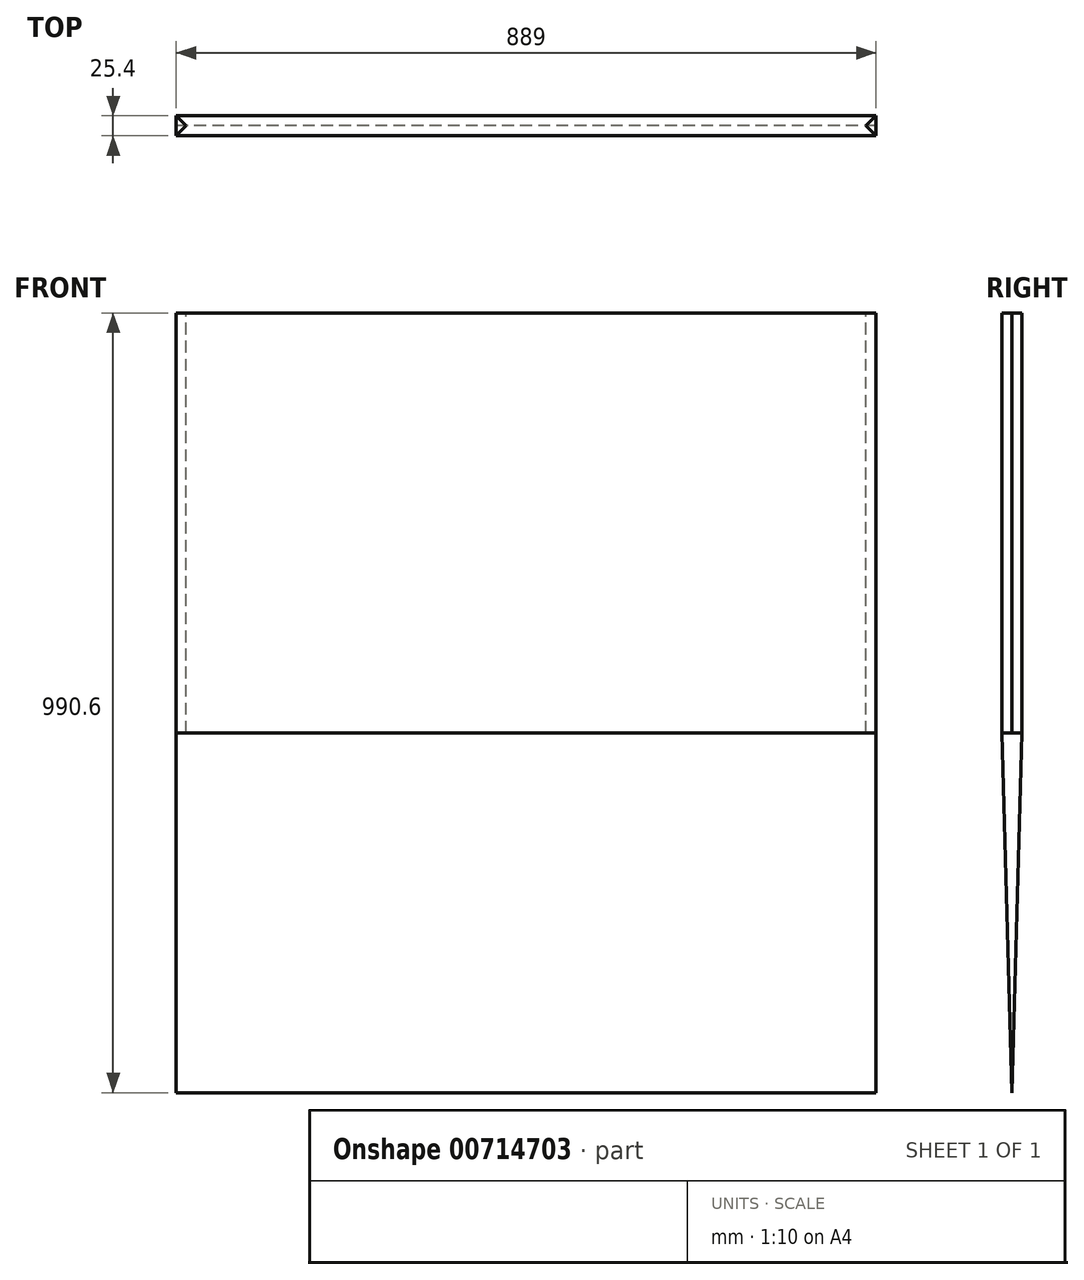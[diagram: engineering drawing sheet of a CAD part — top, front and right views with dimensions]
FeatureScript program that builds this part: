
annotation { "Feature Type Name" : "Feature", "Feature Type Description" : "" }
export const myFeature = defineFeature(function(context is Context, id is Id, definition is map)
    precondition{}
    {
        {
            var Q0;
            Q0=qCreatedBy(makeId("Top.planeOp"),FACE);
            var sketch = newSketch(context, id + "F0", { "sketchPlane" : qUnion([Q0])});
            skLineSegment(sketch, "E0", {"start": v(0, 25.4) * mm, "end": v(889, 25.4) * mm});
            skLineSegment(sketch, "E1", {"start": v(889, 25.4) * mm, "end": v(876.3, 12.7) * mm});
            skLineSegment(sketch, "E2", {"start": v(876.3, 12.7) * mm, "end": v(889, 0) * mm});
            skLineSegment(sketch, "E3", {"start": v(889, 0) * mm, "end": v(0, 0) * mm});
            skLineSegment(sketch, "E4", {"start": v(0, 0) * mm, "end": v(12.7, 12.7) * mm});
            skLineSegment(sketch, "E5", {"start": v(12.7, 12.7) * mm, "end": v(0, 25.4) * mm});
            skLineSegment(sketch, "E6", {"start": v(0, 25.4) * mm, "end": v(127, 25.4) * mm});
            skSolve(sketch);
        }
        {
            var Q0;
            Q0=makeQuery(id+"F0.imprint","IMPRINT",FACE,{"disambiguationData":[TD([[makeQuery(id+"F0.imprint","IMPRINT",EDGE,{"derivedFrom":sQuery(id+"F0.wireOp",EDGE,"E1")}),-1.0]])]});
            extrude(context, id + "F1", {"entities" : qUnion([Q0]), "oppositeDirection" : true, "depth" : 533.4 * mm, "offsetDistance" : 25.4 * mm});
        }
        {
            var Q0;
            Q0=qCreatedBy(makeId("Right.planeOp"),FACE);
            var sketch = newSketch(context, id + "F2", { "sketchPlane" : qUnion([Q0])});
            skLineSegment(sketch, "E7", {"start": v(0, -533.4) * mm, "end": v(25.4, -533.4) * mm});
            skLineSegment(sketch, "E8", {"start": v(25.4, -533.4) * mm, "end": v(12.7, -990.6) * mm});
            skLineSegment(sketch, "E9", {"start": v(12.7, -990.6) * mm, "end": v(0, -533.4) * mm});
            skSolve(sketch);
        }
        {
            var Q0;
            Q0 = qSketchRegion(id + "F2", true);
            var Q1;
            Q1=makeQuery(id+"F2.imprint","IMPRINT",FACE,{"disambiguationData":[TD([[makeQuery(id+"F2.imprint","IMPRINT",EDGE,{"derivedFrom":sQuery(id+"F2.wireOp",EDGE,"E7")}),-1.0]])]});
            extrude(context, id + "F3", {"entities" : qUnion([Q0, Q1]), "depth" : 889 * mm, "offsetDistance" : 25.4 * mm});
        }
    });
